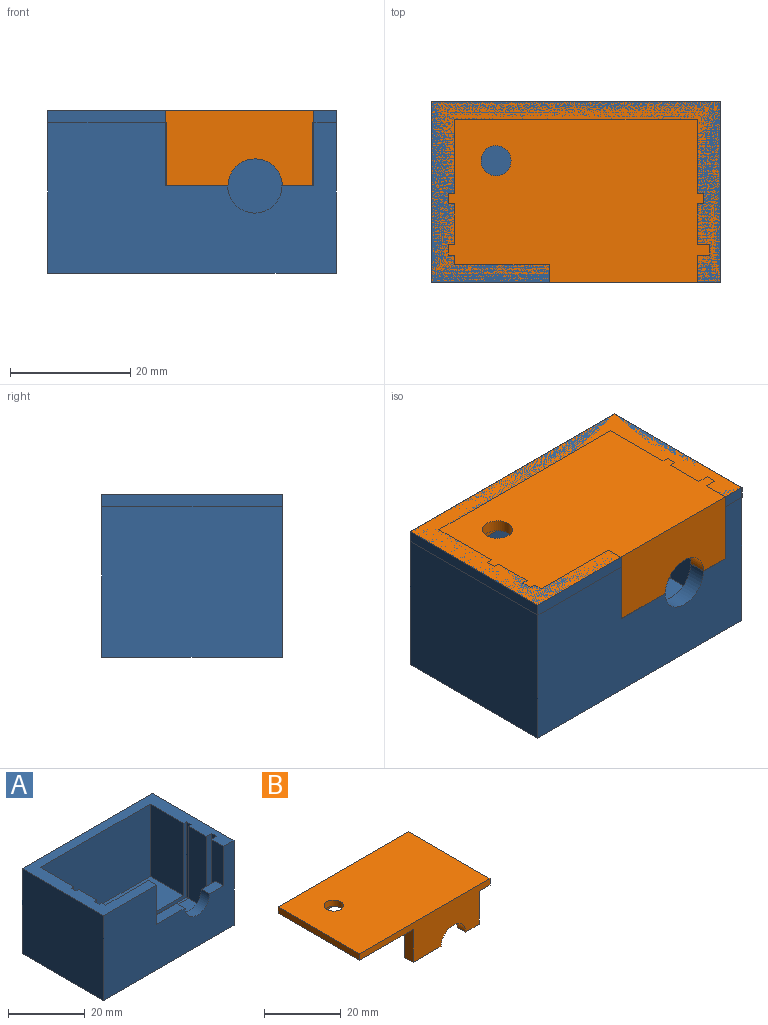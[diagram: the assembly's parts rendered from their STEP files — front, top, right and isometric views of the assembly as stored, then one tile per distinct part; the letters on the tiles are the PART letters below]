
ASSEMBLY  parts=2 mates=1
PART A: 31 faces, bbox 47.9x30x27 mm
  f0: plane 5.2x3mm, normal (0,0,1), area 15.6mm2, adj f1,f2,f15,f30
  f1: plane 40.3x23mm, normal (0,1,0), area 588.1mm2, adj f0,f2,f16,f17,f22,f24,f29,f30
  f2: plane 23x4.5mm, normal (-1,0,0), area 72mm2, adj f0,f1,f15,f18,f22,f24
  f3: plane 24x1.7mm, normal (1,0,0), area 40.8mm2, adj f7,f9,f22,f28
  f4: plane 23x12.3mm, normal (1,0,0), area 282.9mm2, adj f5,f7,f22,f26
  f5: plane 40.3x23mm, normal (0,-1,0), area 926.9mm2, adj f4,f6,f22,f26
  f6: plane 23x12.3mm, normal (-1,0,0), area 282.9mm2, adj f5,f7,f22,f26
  f7: plane 42.3x24mm, normal (0,-1,0), area 88.3mm2, adj f3,f4,f6,f8,f22,f26,f28
  f8: plane 24x1.7mm, normal (-1,0,0), area 40.8mm2, adj f7,f9,f22,f28
  f9: plane 42.3x24mm, normal (0,1,0), area 88.3mm2, adj f3,f8,f10,f21,f22,f25,f28
  f10: plane 23x6.7mm, normal (-1,0,0), area 154.1mm2, adj f9,f20,f22,f25
  f11: plane 24x1.8mm, normal (-1,0,0), area 43.2mm2, adj f18,f20,f22,f27
  f12: plane 30x27mm, normal (1,0,0), area 810mm2, adj f13,f15,f22,f23
  f13: plane 47.9x27mm, normal (0,1,0), area 1293.3mm2, adj f12,f14,f22,f23
  f14: plane 30x27mm, normal (-1,0,0), area 810mm2, adj f13,f15,f22,f23
  f15: plane 47.9x27mm, normal (0,-1,0), area 954.5mm2, adj f0,f2,f12,f14,f16,f22,f23,f29
  f16: plane 12.5x3mm, normal (1,0,0), area 37.5mm2, adj f1,f15,f22,f29
  f17: plane 23x1.5mm, normal (1,0,0), area 34.5mm2, adj f1,f18,f22,f24
  f18: plane 43.3x24mm, normal (0,1,0), area 112.3mm2, adj f2,f11,f17,f19,f22,f24,f27
  f19: plane 24x1.8mm, normal (1,0,0), area 43.2mm2, adj f18,f20,f22,f27
  f20: plane 43.3x24mm, normal (0,-1,0), area 112.3mm2, adj f10,f11,f19,f21,f22,f25,f27
  f21: plane 23x6.7mm, normal (1,0,0), area 154.1mm2, adj f9,f20,f22,f25
  f22: plane 47.9x30mm, normal (0,0,1), area 387.3mm2, adj f1,f2,f3,f4,f5,f6,f7,f8
  f23: plane 47.9x30mm, normal (0,0,-1), area 1437mm2, adj f12,f13,f14,f15
  f24: plane 40.3x1.5mm, normal (0,0,1), area 60.5mm2, adj f1,f2,f17,f18
  f25: plane 40.3x6.7mm, normal (0,0,1), area 270mm2, adj f9,f10,f20,f21
  f26: plane 40.3x12.3mm, normal (0,0,1), area 495.7mm2, adj f4,f5,f6,f7
  f27: plane 43.3x1.8mm, normal (0,0,1), area 77.9mm2, adj f11,f18,f19,f20
  f28: plane 42.3x1.7mm, normal (0,0,1), area 71.9mm2, adj f3,f7,f8,f9
  f29: plane 10.36x3mm, normal (0,0,1), area 31.1mm2, adj f1,f15,f16,f30
  f30: cylinder r=4.5mm len=9mm, axis (0,-1,0), area 42.4mm2, adj f0,f1,f15,f29
PART B: 37 faces, bbox 47.9x30x12.5 mm
  f0: plane 24.36x10.5mm, normal (0,1,0), area 223.9mm2, adj f1,f2,f3,f5,f7,f17
  f1: plane 10.5x3mm, normal (1,0,0), area 31.5mm2, adj f0,f3,f4,f17
  f2: plane 10.5x3mm, normal (-1,0,0), area 31.5mm2, adj f0,f4,f5,f17
  f3: plane 5.1x3mm, normal (0,0,-1), area 15.3mm2, adj f0,f1,f4,f7
  f4: plane 47.9x12.5mm, normal (0,-1,0), area 319.7mm2, adj f1,f2,f3,f5,f6,f7,f13,f15
  f5: plane 10.26x3mm, normal (0,0,-1), area 30.8mm2, adj f0,f2,f4,f7
  f6: plane 47.9x30mm, normal (0,0,1), area 1417.4mm2, adj f4,f13,f14,f15,f16
  f7: cylinder r=4.5mm len=9mm, axis (0,-1,0), area 42.4mm2, adj f0,f3,f4,f5
  f8: plane 6.7x3mm, normal (1,0,0), area 20.1mm2, adj f9,f11,f12,f17
  f9: plane 3x1.9mm, normal (0,1,0), area 5.7mm2, adj f8,f10,f12,f17
  f10: plane 6.7x3mm, normal (-1,0,0), area 20.1mm2, adj f9,f11,f12,f17
  f11: plane 3x1.9mm, normal (0,-1,0), area 5.7mm2, adj f8,f10,f12,f17
  f12: plane 6.7x1.9mm, normal (0,0,-1), area 12.7mm2, adj f8,f9,f10,f11
  f13: plane 30x2mm, normal (1,0,0), area 60mm2, adj f4,f6,f14,f17
  f14: plane 47.9x2mm, normal (0,1,0), area 95.8mm2, adj f6,f13,f15,f17
  f15: plane 30x2mm, normal (-1,0,0), area 60mm2, adj f4,f6,f14,f17
  f16: cylinder r=2.5mm len=5mm, axis (0,0,1), area 31.4mm2, adj f6,f17
  f17: plane 47.9x30mm, normal (0,0,-1), area 1181.6mm2, adj f0,f1,f2,f4,f8,f9,f10,f11
  f18: plane 40.1x12.2mm, normal (0,0,-1), area 115.3mm2, adj f19,f20,f21,f22,f23,f24,f25,f26
  f19: plane 3x1.9mm, normal (0,-1,0), area 5.7mm2, adj f17,f18,f20,f25
  f20: plane 10.3x3mm, normal (-1,0,0), area 30.9mm2, adj f17,f18,f19,f26
  f21: plane 10.3x3mm, normal (1,0,0), area 30.9mm2, adj f17,f18,f22,f26
  f22: plane 3x1.9mm, normal (0,-1,0), area 5.7mm2, adj f17,f18,f21,f23
  f23: plane 12.2x3mm, normal (-1,0,0), area 36.6mm2, adj f17,f18,f22,f24
  f24: plane 40.1x3mm, normal (0,1,0), area 120.3mm2, adj f17,f18,f23,f25
  f25: plane 12.2x3mm, normal (1,0,0), area 36.6mm2, adj f17,f18,f19,f24
  f26: plane 36.3x3mm, normal (0,-1,0), area 108.9mm2, adj f17,f18,f20,f21
  f27: plane 6.7x1.9mm, normal (0,0,-1), area 12.7mm2, adj f28,f29,f30,f31
  f28: plane 3x1.9mm, normal (0,-1,0), area 5.7mm2, adj f17,f27,f29,f31
  f29: plane 6.7x3mm, normal (-1,0,0), area 20.1mm2, adj f17,f27,f28,f30
  f30: plane 3x1.9mm, normal (0,1,0), area 5.7mm2, adj f17,f27,f29,f31
  f31: plane 6.7x3mm, normal (1,0,0), area 20.1mm2, adj f17,f27,f28,f30
  f32: plane 15.64x3mm, normal (0,-1,0), area 46.9mm2, adj f17,f33,f35,f36
  f33: plane 3x1.4mm, normal (1,0,0), area 4.2mm2, adj f17,f32,f34,f36
  f34: plane 15.64x3mm, normal (0,1,0), area 46.9mm2, adj f17,f33,f35,f36
  f35: plane 3x1.4mm, normal (-1,0,0), area 4.2mm2, adj f17,f32,f34,f36
  f36: plane 15.64x1.4mm, normal (0,0,-1), area 21.9mm2, adj f32,f33,f34,f35
PLACE A t=(-105.1,45.91,-10.15)mm
PLACE B t=(-32.66,18.24,16.85)mm
MATE fastened B.f3 <-> A.f0  axis (0,0,-1) through (-18.62,9.77,4.35)mm
